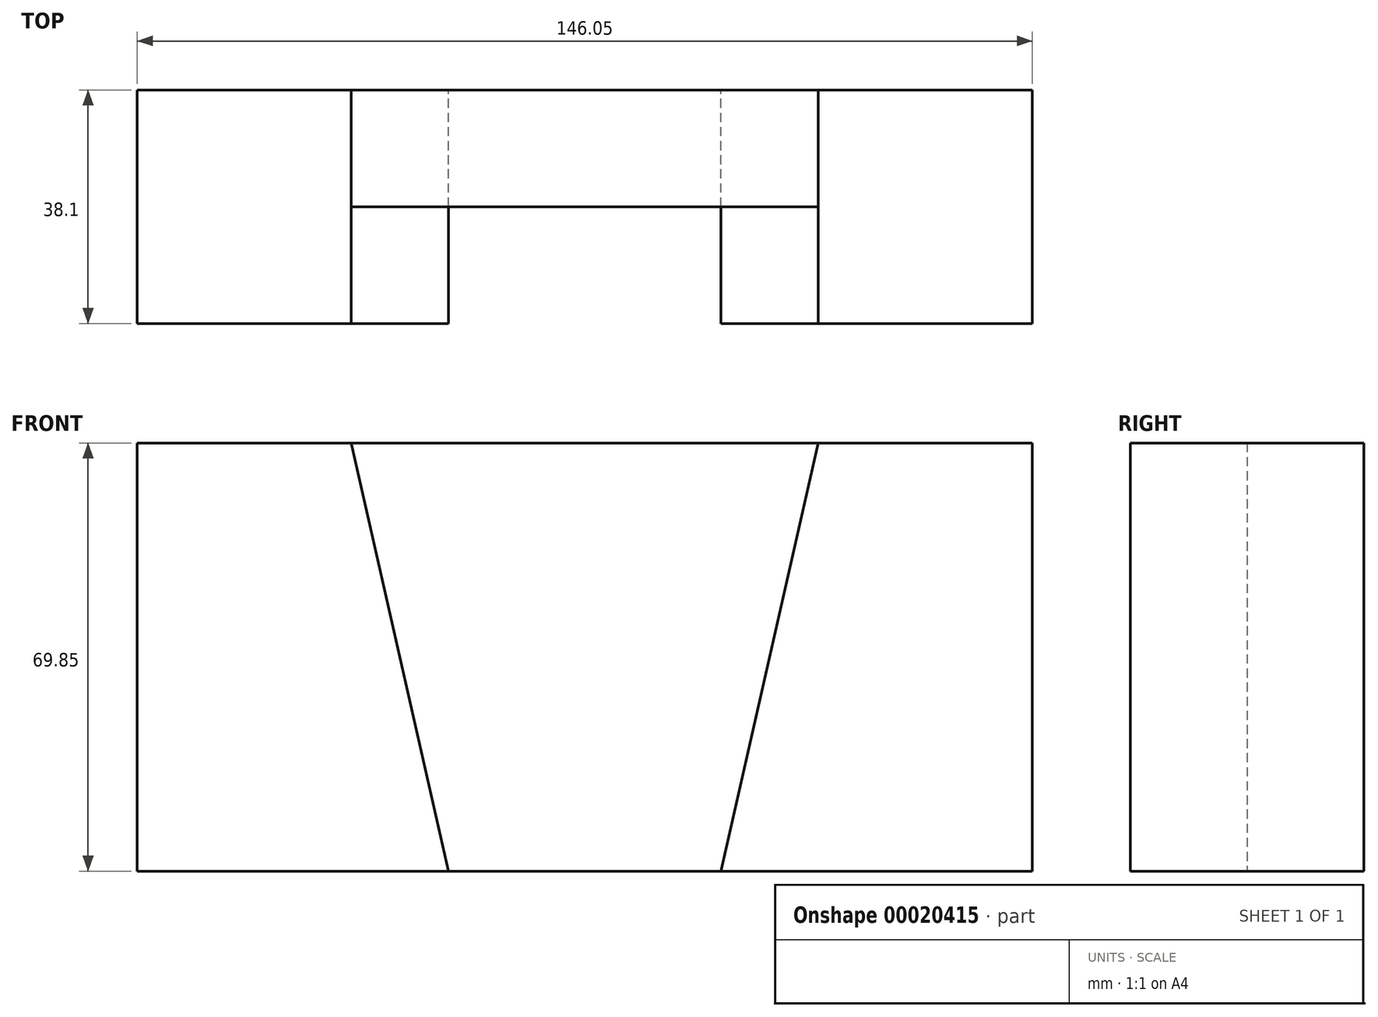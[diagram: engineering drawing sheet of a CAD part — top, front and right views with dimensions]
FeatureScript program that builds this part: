
annotation { "Feature Type Name" : "Feature", "Feature Type Description" : "" }
export const myFeature = defineFeature(function(context is Context, id is Id, definition is map)
    precondition{}
    {
        {
            var Q0;
            Q0=qCreatedBy(makeId("Front.planeOp"),FACE);
            var sketch = newSketch(context, id + "F0", { "sketchPlane" : qUnion([Q0])});
            skLineSegment(sketch, "E0.bottom", {"start": v(-66.63, 28) * mm, "end": v(79.42, 28) * mm});
            skLineSegment(sketch, "E0.top", {"start": v(-66.63, -41.85) * mm, "end": v(79.42, -41.85) * mm});
            skLineSegment(sketch, "E0.left", {"start": v(-66.63, 28) * mm, "end": v(-66.63, -41.85) * mm});
            skLineSegment(sketch, "E0.right", {"start": v(79.42, 28) * mm, "end": v(79.42, -41.85) * mm});
            skLineSegment(sketch, "E1", {"start": v(44.5, 28) * mm, "end": v(28.62, -41.85) * mm});
            skLineSegment(sketch, "E2", {"start": v(-31.7, 28) * mm, "end": v(-15.83, -41.85) * mm});
            skSolve(sketch);
        }
        {
            var Q0;
            {var subQ1=sQuery(id+"F0.wireOp",EDGE,"E0.left");Q0=makeQuery(id+"F0.imprint","IMPRINT",FACE,{"disambiguationData":[TD([[makeQuery(id+"F0.imprint","IMPRINT",EDGE,{"derivedFrom":subQ1}),1.0]])]});}
            var Q1;
            {var subQ1=sQuery(id+"F0.wireOp",EDGE,"E0.right");Q1=makeQuery(id+"F0.imprint","IMPRINT",FACE,{"disambiguationData":[TD([[makeQuery(id+"F0.imprint","IMPRINT",EDGE,{"derivedFrom":subQ1}),-1.0]])]});}
            extrude(context, id + "F1", {"entities" : qUnion([Q0, Q1]), "depth" : 38.1 * mm});
        }
        {
            var Q0;
            {var subQ1=sQuery(id+"F0.wireOp",EDGE,"E1");Q0=makeQuery(id+"F0.imprint","IMPRINT",FACE,{"disambiguationData":[TD([[makeQuery(id+"F0.imprint","IMPRINT",EDGE,{"derivedFrom":subQ1}),-1.0]])]});}
            extrude(context, id + "F2", {"entities" : qUnion([Q0]), "depth" : 19.05 * mm});
        }
    });
